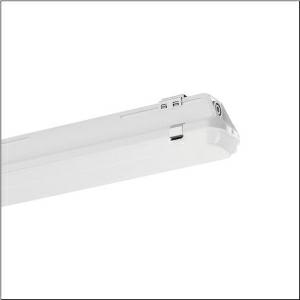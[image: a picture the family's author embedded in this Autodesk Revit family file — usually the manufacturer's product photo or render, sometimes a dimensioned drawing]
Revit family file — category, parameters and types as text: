
# Revit family: monsun_r__11_51fp109p460h_b614
name_source: partatom
category: Lighting Fixtures
units: mm (PartAtom-declared; Revit-internal decimal feet)

## family parameters
Cut with Voids When Loaded = No
Host = Face
Light Source = No
Part Type = Normal
Room Calculation Point = No
Round Connector Dimension = Use Diameter
Shared = No

## types (1)
- Monsun® 11 (1 x LED, 6100 lm, 34 W, 4000K)
    Apparent Load = 34 VA
    CIE Flux Codes = 47 77 93 94 100
    Color Rendering = 80
    Color Temperature = 4000K
    Default Elevation = 1800 mm
    Description = Monsun® 11, damp-proof luminaire, chain hanger, primary optical cover: enclosure, of PMMA, light emission: direct distribution, primary light characteristic: symmetric, installation type: suspended mounting, surface-mounted, horizontal mounting, vertical mounting, LED, rated luminous flux: 6.100lm, luminous efficacy: 179lm/W, light colour: 840, colour temperature: 4000K, control gear: ON/OFF, CLOi, with terminal, 3-pole, max. 2.5mm², mains connection: 220..240V, AC, 50/60Hz, start of lifetime: 34W, end of service life: 38W, luminaire housing, of glass-fibre reinforced polyester, uncoated, bright grey, incl. chain hanger, length: 1.590mm, width: 90mm, height: 88mm, clip for enclosure, of stainless steel (V2A), ceiling mounting element, of stainless steel (V2A), chain hanger, of stainless steel (V2A), protection rating (complete): IP66, insulation class (complete): insulation class I (protective earthing), certification: CE, ENEC, VDE, UKCA, protection symbol: D, impact resistance: IK04, permissible operating ambient temperature: -35..+40°C, standard: EN 50419, EN 60598-2-1, no direct snow, no direct sun, no direct rain, for indoor or canopied outdoor use, corresponds to IFS (International Featured Standards) requirements for safety and quality in the food industry, contact your sales advisor before using the luminaires in applications with unclear chemical exposure, large temperature fluctuations or condensation-forming humidity, LABS conformity tested according to VDMA 24364:2018-05, packaging unit: 1 piece
    Height = 89 mm
    Lamp = 1 x LED
    Lamp Light Flux = 6100 lm
    Lamp Power = 34 W
    Lamp count = 1
    Length = 1590 mm
    Luminous efficacy = 179 lm/W
    Manufacturer = Siteco
    ModVariant = No
    Model = 51FP109P460H
    Mounting Place = Ceiling
    Mounting Type = Surface mounted
    Number of Poles = 1
    OnlyDefault = Yes
    Power Factor = 1
    Product Name = Monsun® 11
    Product group = damp-proof luminaire
    ProductGroupID = 300
    Protection Class = Protection class I
    Protection Degree = IP 66
    RLX_Detail_Level = 1
    RLX_Emergency_Light_Flux = 0 lm
    RLX_Emergency_Type = 0
    RLX_Emergency_Type_DB = No
    RlxData = <blob elided: 88701 chars, md5=cc4675c6>
    Socket = socket
    Standby Power = 0 W
    System Light Flux = 6100 lm
    System Power = 34 W
    Type Comments = Product without accessories
    Type Image = l_1349237.jpg
    URL = http://relux.com
    VarID = ---
    Voltage = 0 V
    Weight = 0.00 kg
    Width = 90 mm

## geometry (parser evidence)
native form markers: Blend x4, Sweep x11
no freeform markers — native parametric forms only
